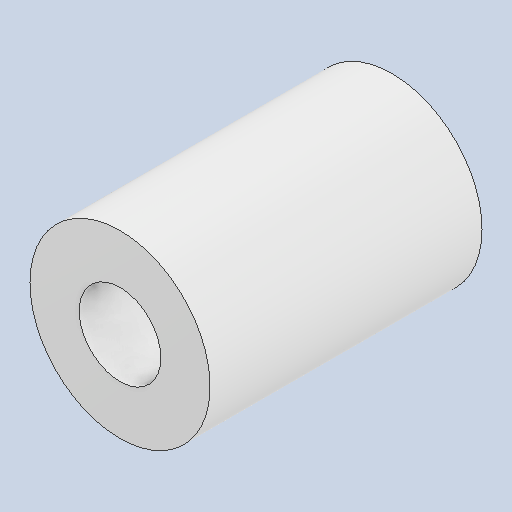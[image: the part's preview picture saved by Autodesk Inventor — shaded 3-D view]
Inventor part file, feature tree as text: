
AUTODESK INVENTOR PART (.ipt)
format: ipt  version: 2023 (Build 270158000, 158)  size: 140,288 bytes
history: native  units: in
note: dims shown in document units (in); Inventor stores cm internally (conversion verified against a paired STEP export)
features: sketch x1, plane x1, extrude x1
ambient origin geometry x8: Origin, YZ Plane, XZ Plane, XY Plane, X Axis, Y Axis, Z Axis, Center Point
bodies: Solid1 (feature_tree)
feature tree (3):
  sketch  "Sketch1"  dims[d0=0.17in d1=0.375in d2=1.0in d3=0.0in]
  plane  "Work Plane1"
  extrude  "Extrusion1"  Depth=0.375in
